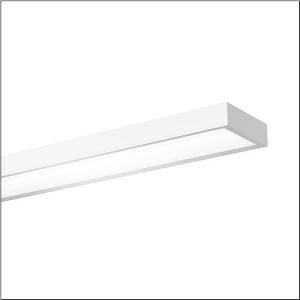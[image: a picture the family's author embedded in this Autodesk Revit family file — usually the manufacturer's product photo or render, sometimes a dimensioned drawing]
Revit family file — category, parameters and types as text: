
# Revit family: sport_31_51hs12dc3dca
name_source: partatom
category: Lighting Fixtures
units: mm (PartAtom-declared; Revit-internal decimal feet)

## family parameters
Cut with Voids When Loaded = No
Host = Face
Light Source = No
Part Type = Normal
Room Calculation Point = No
Round Connector Dimension = Use Diameter
Shared = No

## types (1)
- --- (1 x LED, 7500 lm, 55.4 W, 3000K)
    Apparent Load = 55 VA
    CIE Flux Codes = 65 89 97 100 100
    Color Rendering = 80
    Color Temperature = 3000K
    Default Elevation = 1800 mm
    Description = Sport 31, LED high bay luminaire, primary light control with reflector, of sheet steel, primary anti-glare with prismatic structure, of PC, primary optical cover: cover panel, of PC, light emission: direct distribution, primary light characteristic: symmetric, installation type: suspended mounting, recessed, surface-mounted, LED, rated luminous flux: 7.500lm, luminous efficacy: 130lm/W, light colour: 830, colour temperature: 3000K, control gear: ECG DALI, with terminal, 5-pole, max. 2.5mm², mains connection: 220..240V, AC/DC, 50/60Hz, rated input power: 58W, housing, of sheet steel, traffic white (RAL 9016), length: 1.540mm, width: 315mm, height: 95mm, protection rating (complete): IP20, protection rating (lamp compartment, on room side): IP50, insulation class (complete): insulation class I (protective earthing), certification: CE, ENEC, UKCA, ball protection: ball impact resistant with ceiling mounting or chain suspension, impact resistance: IK08, permissible operating ambient temperature: -20..+35°C, standard: DIN 18032-3, EN 60598-2-22, packaging unit: 1 piece
    Height = 100 mm  [stored 0.328084 ft]
    Lamp = 1 x LED
    Lamp Light Flux = 7500 lm
    Lamp Power = 55.4 W
    Lamp count = 1
    Length = 1500 mm
    Luminous efficacy = 135 lm/W
    Manufacturer = Siteco
    ModVariant = No
    Model = 51HS12DC3DCA
    Mounting Place = Ceiling
    Mounting Type = Pendant
    Number of Poles = 1
    OnlyDefault = Yes
    Power Factor = 1
    Product Name = Sport 31
    Product group = LED high bay luminaire
    ProductGroupID = 903
    Protection Class = Protection class I
    Protection Degree = IP 20
    RLX_Detail_Level = 1
    RLX_Emergency_Light_Flux = 0 lm
    RLX_Emergency_Type = 0
    RLX_Emergency_Type_DB = No
    RlxData = <blob elided: 22757 chars, md5=b6d62a9e>
    Socket = socket
    Standby Power = 0 W
    System Light Flux = 7500 lm
    System Power = 55 W
    Type Comments = factory setting: luminous flux: 100 % | dim-lin: 254 | 234 mA
    Type Image = l_1006823.jpg
    URL = http://relux.com
    VarID = @adj_151041
    Voltage = 0 V
    Weight = 0.00 kg
    Width = 315 mm

note: [stored X ft] marks values corroborated as IEEE doubles in the binary element streams (Revit-internal decimal feet)

## geometry (parser evidence)
native form markers: Blend x4, Sweep x9
no freeform markers — native parametric forms only
